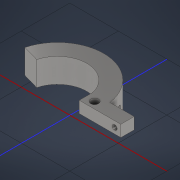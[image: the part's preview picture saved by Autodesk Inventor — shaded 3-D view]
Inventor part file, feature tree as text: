
AUTODESK INVENTOR PART (.ipt)
format: ipt  version: 2021 (Build 250183000, 183)  size: 167,936 bytes
history: native  units: mm
features: sketch x6, extrude x4, hole x2, projected_geometry x2, plane x1, split x1, fillet x1
ambient origin geometry x8: Origin, YZ Plane, XZ Plane, XY Plane, X Axis, Y Axis, Z Axis, Center Point
bodies: Solid1 (feature_tree)
feature tree (17):
  extrude  "Extrusion1"  Depth=12.0mm
  plane  "Work Plane1"
  split  "Split1"
  extrude  "Extrusion2"  TaperAngle=0.0deg  [1 undecoded]
  extrude  "Extrusion3"  TaperAngle=0.0deg  [1 undecoded]
  hole  "Hole1"  [1 undecoded]
  extrude  "halfCut"  Depth=10.0mm TaperAngle=0.0deg
  fillet  "Fillet1"  Radius=10.0mm
  hole  "Hole2"  [1 undecoded]
  sketch  "Sketch1"  dims[d0=12.0mm d2=3.0mm]
  sketch  "Sketch2"  dims[d3=12.0mm d4=0.0mm]
  projected_geometry  "Projected Loop1"
  sketch  "Sketch3"  dims[d5=5.0mm d6=0.0mm]
  projected_geometry  "Projected Loop2"
  sketch  "Sketch4"  dims[d7=7.0mm d8=10.0mm d9=0.0mm]
  sketch  "Sketch5"  dims[d10=-2.75mm d11=5.5mm d12=0.0mm d13=10.0mm d14=0.0mm]
  sketch  "Sketch6"  dims[d15=0.0mm d16=3.559644mm d17=7.119287mm d18=3.25mm d19=6.0mm d20=4.0mm d21=2.0mm d22=90.0deg d23=8.0mm d24=20.594885mm d26=5.5mm d27=0.0mm d28=1.0mm d29=5.25mm d30=6.5mm d31=20.0mm d32=0.0mm d33=2.375mm d34=4.75mm d35=2.5mm d36=2.0mm d37=6.0mm d38=4.0mm d39=2.0mm d40=90.0deg d41=8.0mm d42=20.594885mm]
note: 4 required parameter values undecoded (feature->parameter linkage not recoverable at this tier; creation-order binding heuristic only, values carry confidence <= 0.55)
